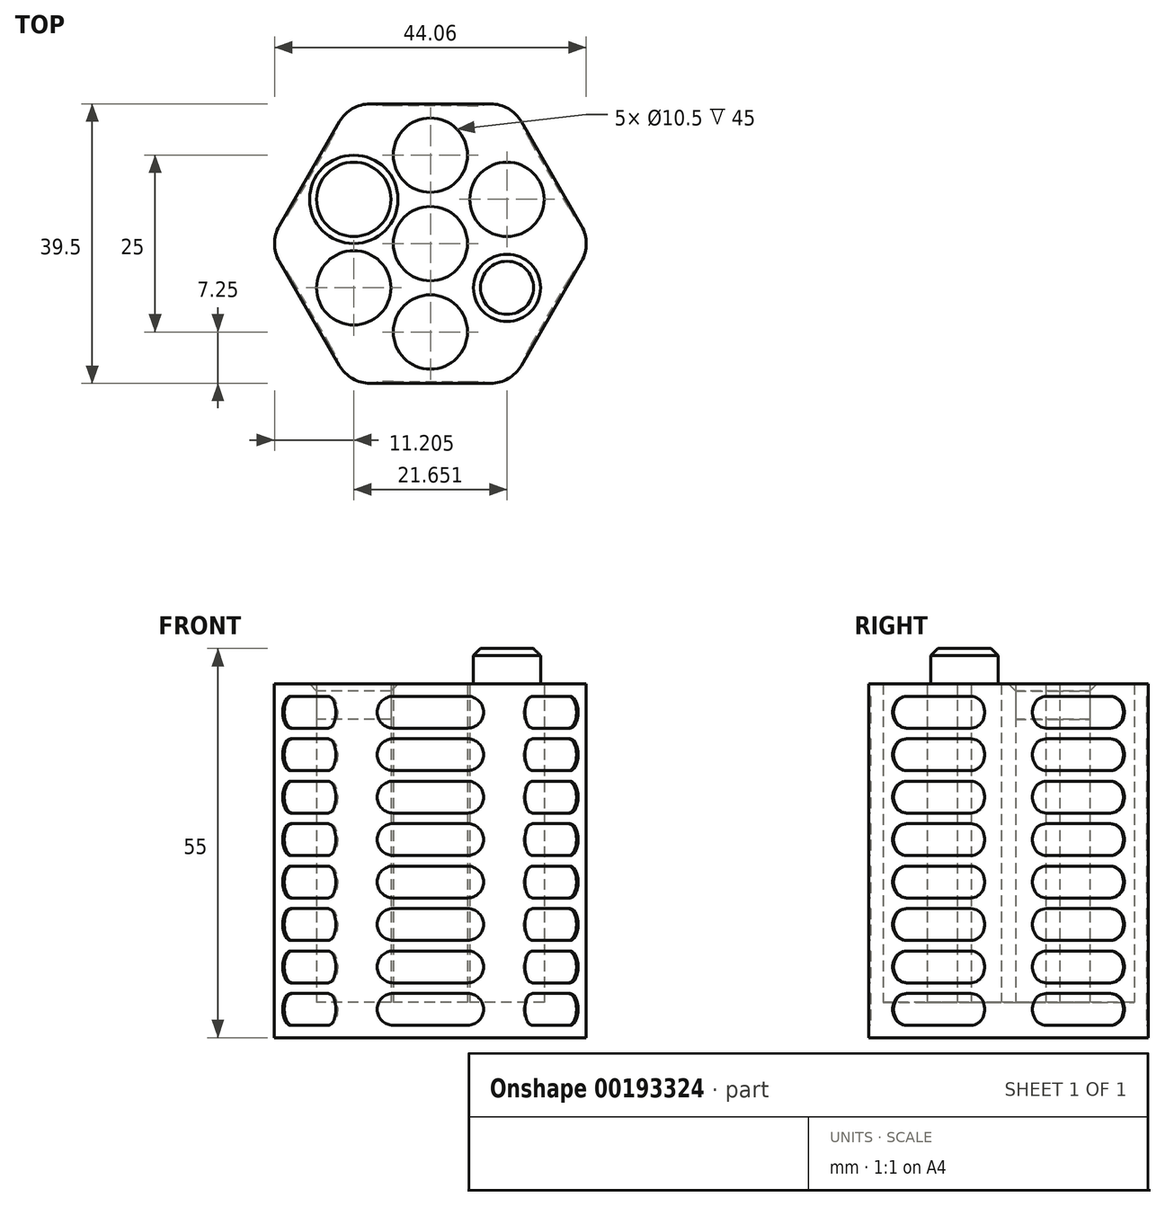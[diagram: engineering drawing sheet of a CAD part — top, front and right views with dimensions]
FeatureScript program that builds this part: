
annotation { "Feature Type Name" : "Feature", "Feature Type Description" : "" }
export const myFeature = defineFeature(function(context is Context, id is Id, definition is map)
    precondition{}
    {
        {
            var Q0;
            Q0=qCreatedBy(makeId("Top.planeOp"),FACE);
            var sketch = newSketch(context, id + "F0", { "sketchPlane" : qUnion([Q0])});
            skPoint(sketch, "E0.0.midPoint", {"position": v(0, 19.75) * mm});
            skCircle(sketch, "E1", {"center": v(0, 12.5) * mm, "radius": 5.25 * mm});
            skPoint(sketch, "E2.center", {"position": v(0, -4.69) * mm});
            skCircle(sketch, "E3.1.0", {"center": v(-10.83, 6.25) * mm, "radius": 5.25 * mm});
            skCircle(sketch, "E3.2.0", {"center": v(-10.83, -6.25) * mm, "radius": 5.25 * mm});
            skCircle(sketch, "E3.3.0", {"center": v(0, -12.5) * mm, "radius": 5.25 * mm});
            skCircle(sketch, "E3.4.0", {"center": v(10.83, -6.25) * mm, "radius": 4.75 * mm});
            skCircle(sketch, "E3.5.0", {"center": v(10.83, 6.25) * mm, "radius": 5.25 * mm});
            skPoint(sketch, "E3.center", {"position": v(0, 0) * mm});
            skCircle(sketch, "E4", {"center": v(0, 0) * mm, "radius": 5.25 * mm});
            skCircle(sketch, "E5.cCircle", {"center": v(0, 0) * mm, "radius": 19.75 * mm, "construction": true});
            skLineSegment(sketch, "E5.0", {"start": v(-11.4, 19.75) * mm, "end": v(11.4, 19.75) * mm});
            skLineSegment(sketch, "E5.1", {"start": v(11.4, 19.75) * mm, "end": v(22.8, 0) * mm});
            skLineSegment(sketch, "E5.2", {"start": v(22.8, 0) * mm, "end": v(11.4, -19.75) * mm});
            skLineSegment(sketch, "E5.3", {"start": v(11.4, -19.75) * mm, "end": v(-11.4, -19.75) * mm});
            skLineSegment(sketch, "E5.4", {"start": v(-11.4, -19.75) * mm, "end": v(-22.8, 0) * mm});
            skLineSegment(sketch, "E5.5", {"start": v(-22.8, 0) * mm, "end": v(-11.4, 19.75) * mm});
            skSolve(sketch);
        }
        {
            var Q0;
            Q0=makeQuery(id+"F0.imprint","IMPRINT",FACE,{"disambiguationData":[TD([[makeQuery(id+"F0.imprint","IMPRINT",EDGE,{"derivedFrom":sQuery(id+"F0.wireOp",EDGE,"E1")}),-1.0]])]});
            extrude(context, id + "F1", {"entities" : qUnion([Q0]), "depth" : 50 * mm});
        }
        {
            var Q0;
            Q0=makeQuery(id+"F0.imprint","IMPRINT",FACE,{"disambiguationData":[TD([[makeQuery(id+"F0.imprint","IMPRINT",EDGE,{"derivedFrom":sQuery(id+"F0.wireOp",EDGE,"E4")}),1.0]])]});
            var Q1;
            Q1=makeQuery(id+"F0.imprint","IMPRINT",FACE,{"disambiguationData":[TD([[makeQuery(id+"F0.imprint","IMPRINT",EDGE,{"derivedFrom":sQuery(id+"F0.wireOp",EDGE,"E1")}),1.0]])]});
            var Q2;
            Q2=makeQuery(id+"F0.imprint","IMPRINT",FACE,{"disambiguationData":[TD([[makeQuery(id+"F0.imprint","IMPRINT",EDGE,{"derivedFrom":sQuery(id+"F0.wireOp",EDGE,"E3.2.0")}),1.0]])]});
            var Q3;
            Q3=makeQuery(id+"F0.imprint","IMPRINT",FACE,{"disambiguationData":[TD([[makeQuery(id+"F0.imprint","IMPRINT",EDGE,{"derivedFrom":sQuery(id+"F0.wireOp",EDGE,"E3.3.0")}),1.0]])]});
            var Q4;
            Q4=makeQuery(id+"F0.imprint","IMPRINT",FACE,{"disambiguationData":[TD([[makeQuery(id+"F0.imprint","IMPRINT",EDGE,{"derivedFrom":sQuery(id+"F0.wireOp",EDGE,"E3.5.0")}),1.0]])]});
            extrude(context, id + "F2", {"entities" : qUnion([Q0, Q1, Q2, Q3, Q4]), "operationType" : NewBodyOperationType.ADD, "depth" : 5 * mm});
        }
        {
            var Q0;
            Q0=makeQuery(id+"F0.imprint","IMPRINT",FACE,{"disambiguationData":[TD([[makeQuery(id+"F0.imprint","IMPRINT",EDGE,{"derivedFrom":sQuery(id+"F0.wireOp",EDGE,"E3.4.0")}),1.0]])]});
            extrude(context, id + "F3", {"entities" : qUnion([Q0]), "operationType" : NewBodyOperationType.ADD, "depth" : 55 * mm});
        }
        {
            var Q0;
            Q0=makeQuery(id+"F0.imprint","IMPRINT",FACE,{"disambiguationData":[TD([[makeQuery(id+"F0.imprint","IMPRINT",EDGE,{"derivedFrom":sQuery(id+"F0.wireOp",EDGE,"E3.1.0")}),1.0]])]});
            extrude(context, id + "F4", {"entities" : qUnion([Q0]), "operationType" : NewBodyOperationType.ADD, "depth" : 45 * mm});
        }
        {
            var Q0;
            Q0=makeQuery(id+"F3.opExtrude","CAP_EDGE",EDGE,{"disambiguationData":[OSD([sQuery(id+"F0.wireOp",EDGE,"E3.4.0")])],"isStart":false});
            var Q1;
            Q1=makeQuery(id+"F1.opExtrude","CAP_EDGE",EDGE,{"disambiguationData":[OSD([sQuery(id+"F0.wireOp",EDGE,"E3.1.0")])],"isStart":false});
            var Q2;
            Q2=makeQuery(id+"F1.opExtrude","CAP_EDGE",EDGE,{"disambiguationData":[OSD([sQuery(id+"F0.wireOp",EDGE,"E3.4.0")])],"isStart":false});
            chamfer(context, id + "F5", {"entities" : qUnion([Q0, Q1, Q2]), "width" : 1 * mm, "tangentPropagation" : true});
        }
        {
            var Q0;
            {var subQ0=sQuery(id+"F0.wireOp",EDGE,"E5.5");var subQ1=sQuery(id+"F0.wireOp",EDGE,"E5.0");Q0=makeQuery(id+"FrbD3DidOZEMZMG_1.boolean.opBoolean","MERGE",EDGE,{"derivedFrom":[makeQuery(id+"F1.opExtrude","SWEPT_EDGE",EDGE,{"disambiguationData":[OSD([subQ1,subQ0])]}),makeQuery(id+"FrbD3DidOZEMZMG_1.opExtrude","SWEPT_EDGE",EDGE,{"disambiguationData":[OSD([subQ1,subQ0])]})]});}
            var Q1;
            {var subQ0=sQuery(id+"F0.wireOp",EDGE,"E5.1");var subQ1=sQuery(id+"F0.wireOp",EDGE,"E5.0");Q1=makeQuery(id+"FrbD3DidOZEMZMG_1.boolean.opBoolean","MERGE",EDGE,{"derivedFrom":[makeQuery(id+"F1.opExtrude","SWEPT_EDGE",EDGE,{"disambiguationData":[OSD([subQ1,subQ0])]}),makeQuery(id+"FrbD3DidOZEMZMG_1.opExtrude","SWEPT_EDGE",EDGE,{"disambiguationData":[OSD([subQ1,subQ0])]})]});}
            var Q2;
            {var subQ0=sQuery(id+"F0.wireOp",EDGE,"E5.2");var subQ1=sQuery(id+"F0.wireOp",EDGE,"E5.1");Q2=makeQuery(id+"FrbD3DidOZEMZMG_1.boolean.opBoolean","MERGE",EDGE,{"derivedFrom":[makeQuery(id+"F1.opExtrude","SWEPT_EDGE",EDGE,{"disambiguationData":[OSD([subQ1,subQ0])]}),makeQuery(id+"FrbD3DidOZEMZMG_1.opExtrude","SWEPT_EDGE",EDGE,{"disambiguationData":[OSD([subQ1,subQ0])]})]});}
            var Q3;
            {var subQ0=sQuery(id+"F0.wireOp",EDGE,"E5.5");var subQ1=sQuery(id+"F0.wireOp",EDGE,"E5.4");Q3=makeQuery(id+"FrbD3DidOZEMZMG_1.boolean.opBoolean","MERGE",EDGE,{"derivedFrom":[makeQuery(id+"F1.opExtrude","SWEPT_EDGE",EDGE,{"disambiguationData":[OSD([subQ1,subQ0])]}),makeQuery(id+"FrbD3DidOZEMZMG_1.opExtrude","SWEPT_EDGE",EDGE,{"disambiguationData":[OSD([subQ1,subQ0])]})]});}
            var Q4;
            {var subQ0=sQuery(id+"F0.wireOp",EDGE,"E5.4");var subQ1=sQuery(id+"F0.wireOp",EDGE,"E5.3");Q4=makeQuery(id+"FrbD3DidOZEMZMG_1.boolean.opBoolean","MERGE",EDGE,{"derivedFrom":[makeQuery(id+"F1.opExtrude","SWEPT_EDGE",EDGE,{"disambiguationData":[OSD([subQ1,subQ0])]}),makeQuery(id+"FrbD3DidOZEMZMG_1.opExtrude","SWEPT_EDGE",EDGE,{"disambiguationData":[OSD([subQ1,subQ0])]})]});}
            var Q5;
            {var subQ0=sQuery(id+"F0.wireOp",EDGE,"E5.3");var subQ1=sQuery(id+"F0.wireOp",EDGE,"E5.2");Q5=makeQuery(id+"FrbD3DidOZEMZMG_1.boolean.opBoolean","MERGE",EDGE,{"derivedFrom":[makeQuery(id+"F1.opExtrude","SWEPT_EDGE",EDGE,{"disambiguationData":[OSD([subQ1,subQ0])]}),makeQuery(id+"FrbD3DidOZEMZMG_1.opExtrude","SWEPT_EDGE",EDGE,{"disambiguationData":[OSD([subQ1,subQ0])]})]});}
            fillet(context, id + "F6", {"entities" : qUnion([Q0, Q1, Q2, Q3, Q4, Q5]), "radius" : 5 * mm, "tangentPropagation" : true, "allowEdgeOverflow" : false});
        }
        {
            var Q0;
            {var subQ0=sQuery(id+"F0.wireOp",EDGE,"E5.3");Q0=makeQuery(id+"FrbD3DidOZEMZMG_1.boolean.opBoolean","MERGE",FACE,{"derivedFrom":[makeQuery(id+"F1.opExtrude","SWEPT_FACE",FACE,{"disambiguationData":[OSD([subQ0])]}),makeQuery(id+"FrbD3DidOZEMZMG_1.opExtrude","SWEPT_FACE",FACE,{"disambiguationData":[OSD([subQ0])]})]});}
            var sketch = newSketch(context, id + "F7", { "sketchPlane" : qUnion([Q0])});
            skLineSegment(sketch, "E6", {"start": v(-5.27, 48.25) * mm, "end": v(5.27, 48.25) * mm});
            skArc(sketch, "E7", {"start": v(5.27, 43.75) * mm, "mid": v(7.52, 46) * mm, "end": v(5.27, 48.25) * mm});
            skLineSegment(sketch, "E8", {"start": v(5.27, 43.75) * mm, "end": v(-5.27, 43.75) * mm});
            skArc(sketch, "E9", {"start": v(-5.27, 48.25) * mm, "mid": v(-7.52, 46) * mm, "end": v(-5.27, 43.75) * mm});
            skArc(sketch, "E10.0.1.0", {"start": v(-5.27, 42.25) * mm, "mid": v(-7.52, 40) * mm, "end": v(-5.27, 37.75) * mm});
            skLineSegment(sketch, "E10.0.1.1", {"start": v(-5.27, 42.25) * mm, "end": v(5.27, 42.25) * mm});
            skArc(sketch, "E10.0.1.2", {"start": v(5.27, 37.75) * mm, "mid": v(7.52, 40) * mm, "end": v(5.27, 42.25) * mm});
            skLineSegment(sketch, "E10.0.1.3", {"start": v(5.27, 37.75) * mm, "end": v(-5.27, 37.75) * mm});
            skArc(sketch, "E10.0.2.0", {"start": v(-5.27, 36.25) * mm, "mid": v(-7.52, 34) * mm, "end": v(-5.27, 31.75) * mm});
            skLineSegment(sketch, "E10.0.2.1", {"start": v(-5.27, 36.25) * mm, "end": v(5.27, 36.25) * mm});
            skArc(sketch, "E10.0.2.2", {"start": v(5.27, 31.75) * mm, "mid": v(7.52, 34) * mm, "end": v(5.27, 36.25) * mm});
            skLineSegment(sketch, "E10.0.2.3", {"start": v(5.27, 31.75) * mm, "end": v(-5.27, 31.75) * mm});
            skArc(sketch, "E10.0.3.0", {"start": v(-5.27, 30.25) * mm, "mid": v(-7.52, 28) * mm, "end": v(-5.27, 25.75) * mm});
            skLineSegment(sketch, "E10.0.3.1", {"start": v(-5.27, 30.25) * mm, "end": v(5.27, 30.25) * mm});
            skArc(sketch, "E10.0.3.2", {"start": v(5.27, 25.75) * mm, "mid": v(7.52, 28) * mm, "end": v(5.27, 30.25) * mm});
            skLineSegment(sketch, "E10.0.3.3", {"start": v(5.27, 25.75) * mm, "end": v(-5.27, 25.75) * mm});
            skArc(sketch, "E10.0.4.0", {"start": v(-5.27, 24.25) * mm, "mid": v(-7.52, 22) * mm, "end": v(-5.27, 19.75) * mm});
            skLineSegment(sketch, "E10.0.4.1", {"start": v(-5.27, 24.25) * mm, "end": v(5.27, 24.25) * mm});
            skArc(sketch, "E10.0.4.2", {"start": v(5.27, 19.75) * mm, "mid": v(7.52, 22) * mm, "end": v(5.27, 24.25) * mm});
            skLineSegment(sketch, "E10.0.4.3", {"start": v(5.27, 19.75) * mm, "end": v(-5.27, 19.75) * mm});
            skArc(sketch, "E10.0.5.0", {"start": v(-5.27, 18.25) * mm, "mid": v(-7.52, 16) * mm, "end": v(-5.27, 13.75) * mm});
            skLineSegment(sketch, "E10.0.5.1", {"start": v(-5.27, 18.25) * mm, "end": v(5.27, 18.25) * mm});
            skArc(sketch, "E10.0.5.2", {"start": v(5.27, 13.75) * mm, "mid": v(7.52, 16) * mm, "end": v(5.27, 18.25) * mm});
            skLineSegment(sketch, "E10.0.5.3", {"start": v(5.27, 13.75) * mm, "end": v(-5.27, 13.75) * mm});
            skArc(sketch, "E10.0.6.0", {"start": v(-5.27, 12.25) * mm, "mid": v(-7.52, 10) * mm, "end": v(-5.27, 7.75) * mm});
            skLineSegment(sketch, "E10.0.6.1", {"start": v(-5.27, 12.25) * mm, "end": v(5.27, 12.25) * mm});
            skArc(sketch, "E10.0.6.2", {"start": v(5.27, 7.75) * mm, "mid": v(7.52, 10) * mm, "end": v(5.27, 12.25) * mm});
            skLineSegment(sketch, "E10.0.6.3", {"start": v(5.27, 7.75) * mm, "end": v(-5.27, 7.75) * mm});
            skArc(sketch, "E10.0.7.0", {"start": v(-5.27, 6.25) * mm, "mid": v(-7.52, 4) * mm, "end": v(-5.27, 1.75) * mm});
            skLineSegment(sketch, "E10.0.7.1", {"start": v(-5.27, 6.25) * mm, "end": v(5.27, 6.25) * mm});
            skArc(sketch, "E10.0.7.2", {"start": v(5.27, 1.75) * mm, "mid": v(7.52, 4) * mm, "end": v(5.27, 6.25) * mm});
            skLineSegment(sketch, "E10.0.7.3", {"start": v(5.27, 1.75) * mm, "end": v(-5.27, 1.75) * mm});
            skLineSegment(sketch, "E10.direction1", {"start": v(-5.27, 43.75) * mm, "end": v(19.73, 43.75) * mm, "construction": true});
            skLineSegment(sketch, "E10.direction2", {"start": v(-5.27, 43.75) * mm, "end": v(-5.27, 37.75) * mm, "construction": true});
            skSolve(sketch);
        }
        {
            var Q0;
            Q0=makeQuery(id+"F7.imprint","IMPRINT",FACE,{"disambiguationData":[TD([[makeQuery(id+"F7.imprint","IMPRINT",EDGE,{"derivedFrom":sQuery(id+"F7.wireOp",EDGE,"E6")}),-1.0]])]});
            var Q1;
            Q1=makeQuery(id+"F7.imprint","IMPRINT",FACE,{"disambiguationData":[TD([[makeQuery(id+"F7.imprint","IMPRINT",EDGE,{"derivedFrom":sQuery(id+"F7.wireOp",EDGE,"E10.0.1.0")}),1.0]])]});
            var Q2;
            Q2=makeQuery(id+"F7.imprint","IMPRINT",FACE,{"disambiguationData":[TD([[makeQuery(id+"F7.imprint","IMPRINT",EDGE,{"derivedFrom":sQuery(id+"F7.wireOp",EDGE,"E10.0.2.0")}),1.0]])]});
            var Q3;
            Q3=makeQuery(id+"F7.imprint","IMPRINT",FACE,{"disambiguationData":[TD([[makeQuery(id+"F7.imprint","IMPRINT",EDGE,{"derivedFrom":sQuery(id+"F7.wireOp",EDGE,"E10.0.3.0")}),1.0]])]});
            var Q4;
            Q4=makeQuery(id+"F7.imprint","IMPRINT",FACE,{"disambiguationData":[TD([[makeQuery(id+"F7.imprint","IMPRINT",EDGE,{"derivedFrom":sQuery(id+"F7.wireOp",EDGE,"E10.0.4.0")}),1.0]])]});
            var Q5;
            Q5=makeQuery(id+"F7.imprint","IMPRINT",FACE,{"disambiguationData":[TD([[makeQuery(id+"F7.imprint","IMPRINT",EDGE,{"derivedFrom":sQuery(id+"F7.wireOp",EDGE,"E10.0.5.0")}),1.0]])]});
            var Q6;
            Q6=makeQuery(id+"F7.imprint","IMPRINT",FACE,{"disambiguationData":[TD([[makeQuery(id+"F7.imprint","IMPRINT",EDGE,{"derivedFrom":sQuery(id+"F7.wireOp",EDGE,"E10.0.6.0")}),1.0]])]});
            var Q7;
            Q7=makeQuery(id+"F7.imprint","IMPRINT",FACE,{"disambiguationData":[TD([[makeQuery(id+"F7.imprint","IMPRINT",EDGE,{"derivedFrom":sQuery(id+"F7.wireOp",EDGE,"E10.0.7.0")}),1.0]])]});
            extrude(context, id + "F8", {"entities" : qUnion([Q0, Q1, Q2, Q3, Q4, Q5, Q6, Q7]), "operationType" : NewBodyOperationType.REMOVE, "oppositeDirection" : true, "depth" : .25 * mm});
        }
        {
            var Q0;
            {var subQ0=sQuery(id+"F0.wireOp",EDGE,"E5.2");Q0=makeQuery(id+"FrbD3DidOZEMZMG_1.boolean.opBoolean","MERGE",FACE,{"derivedFrom":[makeQuery(id+"F1.opExtrude","SWEPT_FACE",FACE,{"disambiguationData":[OSD([subQ0])]}),makeQuery(id+"FrbD3DidOZEMZMG_1.opExtrude","SWEPT_FACE",FACE,{"disambiguationData":[OSD([subQ0])]})]});}
            var sketch = newSketch(context, id + "F9", { "sketchPlane" : qUnion([Q0])});
            skLineSegment(sketch, "E11", {"start": v(-5.27, 48.25) * mm, "end": v(5.27, 48.25) * mm});
            skArc(sketch, "E12", {"start": v(5.27, 43.75) * mm, "mid": v(7.52, 46) * mm, "end": v(5.27, 48.25) * mm});
            skLineSegment(sketch, "E13", {"start": v(5.27, 43.75) * mm, "end": v(-5.27, 43.75) * mm});
            skArc(sketch, "E14", {"start": v(-5.27, 48.25) * mm, "mid": v(-7.52, 46) * mm, "end": v(-5.27, 43.75) * mm});
            skArc(sketch, "E15.0.1.0", {"start": v(-5.27, 42.25) * mm, "mid": v(-7.52, 40) * mm, "end": v(-5.27, 37.75) * mm});
            skLineSegment(sketch, "E15.0.1.1", {"start": v(-5.27, 42.25) * mm, "end": v(5.27, 42.25) * mm});
            skArc(sketch, "E15.0.1.2", {"start": v(5.27, 37.75) * mm, "mid": v(7.52, 40) * mm, "end": v(5.27, 42.25) * mm});
            skLineSegment(sketch, "E15.0.1.3", {"start": v(5.27, 37.75) * mm, "end": v(-5.27, 37.75) * mm});
            skArc(sketch, "E15.0.2.0", {"start": v(-5.27, 36.25) * mm, "mid": v(-7.52, 34) * mm, "end": v(-5.27, 31.75) * mm});
            skLineSegment(sketch, "E15.0.2.1", {"start": v(-5.27, 36.25) * mm, "end": v(5.27, 36.25) * mm});
            skArc(sketch, "E15.0.2.2", {"start": v(5.27, 31.75) * mm, "mid": v(7.52, 34) * mm, "end": v(5.27, 36.25) * mm});
            skLineSegment(sketch, "E15.0.2.3", {"start": v(5.27, 31.75) * mm, "end": v(-5.27, 31.75) * mm});
            skArc(sketch, "E15.0.3.0", {"start": v(-5.27, 30.25) * mm, "mid": v(-7.52, 28) * mm, "end": v(-5.27, 25.75) * mm});
            skLineSegment(sketch, "E15.0.3.1", {"start": v(-5.27, 30.25) * mm, "end": v(5.27, 30.25) * mm});
            skArc(sketch, "E15.0.3.2", {"start": v(5.27, 25.75) * mm, "mid": v(7.52, 28) * mm, "end": v(5.27, 30.25) * mm});
            skLineSegment(sketch, "E15.0.3.3", {"start": v(5.27, 25.75) * mm, "end": v(-5.27, 25.75) * mm});
            skArc(sketch, "E15.0.4.0", {"start": v(-5.27, 24.25) * mm, "mid": v(-7.52, 22) * mm, "end": v(-5.27, 19.75) * mm});
            skLineSegment(sketch, "E15.0.4.1", {"start": v(-5.27, 24.25) * mm, "end": v(5.27, 24.25) * mm});
            skArc(sketch, "E15.0.4.2", {"start": v(5.27, 19.75) * mm, "mid": v(7.52, 22) * mm, "end": v(5.27, 24.25) * mm});
            skLineSegment(sketch, "E15.0.4.3", {"start": v(5.27, 19.75) * mm, "end": v(-5.27, 19.75) * mm});
            skArc(sketch, "E15.0.5.0", {"start": v(-5.27, 18.25) * mm, "mid": v(-7.52, 16) * mm, "end": v(-5.27, 13.75) * mm});
            skLineSegment(sketch, "E15.0.5.1", {"start": v(-5.27, 18.25) * mm, "end": v(5.27, 18.25) * mm});
            skArc(sketch, "E15.0.5.2", {"start": v(5.27, 13.75) * mm, "mid": v(7.52, 16) * mm, "end": v(5.27, 18.25) * mm});
            skLineSegment(sketch, "E15.0.5.3", {"start": v(5.27, 13.75) * mm, "end": v(-5.27, 13.75) * mm});
            skArc(sketch, "E15.0.6.0", {"start": v(-5.27, 12.25) * mm, "mid": v(-7.52, 10) * mm, "end": v(-5.27, 7.75) * mm});
            skLineSegment(sketch, "E15.0.6.1", {"start": v(-5.27, 12.25) * mm, "end": v(5.27, 12.25) * mm});
            skArc(sketch, "E15.0.6.2", {"start": v(5.27, 7.75) * mm, "mid": v(7.52, 10) * mm, "end": v(5.27, 12.25) * mm});
            skLineSegment(sketch, "E15.0.6.3", {"start": v(5.27, 7.75) * mm, "end": v(-5.27, 7.75) * mm});
            skArc(sketch, "E15.0.7.0", {"start": v(-5.27, 6.25) * mm, "mid": v(-7.52, 4) * mm, "end": v(-5.27, 1.75) * mm});
            skLineSegment(sketch, "E15.0.7.1", {"start": v(-5.27, 6.25) * mm, "end": v(5.27, 6.25) * mm});
            skArc(sketch, "E15.0.7.2", {"start": v(5.27, 1.75) * mm, "mid": v(7.52, 4) * mm, "end": v(5.27, 6.25) * mm});
            skLineSegment(sketch, "E15.0.7.3", {"start": v(5.27, 1.75) * mm, "end": v(-5.27, 1.75) * mm});
            skLineSegment(sketch, "E15.direction1", {"start": v(-5.27, 43.75) * mm, "end": v(20.73, 43.75) * mm, "construction": true});
            skLineSegment(sketch, "E15.direction2", {"start": v(-5.27, 43.75) * mm, "end": v(-5.27, 37.75) * mm, "construction": true});
            skSolve(sketch);
        }
        {
            var Q0;
            Q0=makeQuery(id+"F9.imprint","IMPRINT",FACE,{"disambiguationData":[TD([[makeQuery(id+"F9.imprint","IMPRINT",EDGE,{"derivedFrom":sQuery(id+"F9.wireOp",EDGE,"E11")}),-1.0]])]});
            var Q1;
            Q1=makeQuery(id+"F9.imprint","IMPRINT",FACE,{"disambiguationData":[TD([[makeQuery(id+"F9.imprint","IMPRINT",EDGE,{"derivedFrom":sQuery(id+"F9.wireOp",EDGE,"E15.0.1.0")}),1.0]])]});
            var Q2;
            Q2=makeQuery(id+"F9.imprint","IMPRINT",FACE,{"disambiguationData":[TD([[makeQuery(id+"F9.imprint","IMPRINT",EDGE,{"derivedFrom":sQuery(id+"F9.wireOp",EDGE,"E15.0.2.0")}),1.0]])]});
            var Q3;
            Q3=makeQuery(id+"F9.imprint","IMPRINT",FACE,{"disambiguationData":[TD([[makeQuery(id+"F9.imprint","IMPRINT",EDGE,{"derivedFrom":sQuery(id+"F9.wireOp",EDGE,"E15.0.3.0")}),1.0]])]});
            var Q4;
            Q4=makeQuery(id+"F9.imprint","IMPRINT",FACE,{"disambiguationData":[TD([[makeQuery(id+"F9.imprint","IMPRINT",EDGE,{"derivedFrom":sQuery(id+"F9.wireOp",EDGE,"E15.0.4.0")}),1.0]])]});
            var Q5;
            Q5=makeQuery(id+"F9.imprint","IMPRINT",FACE,{"disambiguationData":[TD([[makeQuery(id+"F9.imprint","IMPRINT",EDGE,{"derivedFrom":sQuery(id+"F9.wireOp",EDGE,"E15.0.5.0")}),1.0]])]});
            var Q6;
            Q6=makeQuery(id+"F9.imprint","IMPRINT",FACE,{"disambiguationData":[TD([[makeQuery(id+"F9.imprint","IMPRINT",EDGE,{"derivedFrom":sQuery(id+"F9.wireOp",EDGE,"E15.0.6.0")}),1.0]])]});
            var Q7;
            Q7=makeQuery(id+"F9.imprint","IMPRINT",FACE,{"disambiguationData":[TD([[makeQuery(id+"F9.imprint","IMPRINT",EDGE,{"derivedFrom":sQuery(id+"F9.wireOp",EDGE,"E15.0.7.0")}),1.0]])]});
            extrude(context, id + "F10", {"entities" : qUnion([Q0, Q1, Q2, Q3, Q4, Q5, Q6, Q7]), "operationType" : NewBodyOperationType.REMOVE, "oppositeDirection" : true, "depth" : .25 * mm});
        }
        {
            var Q0;
            {var subQ0=sQuery(id+"F0.wireOp",EDGE,"E5.1");Q0=makeQuery(id+"FrbD3DidOZEMZMG_1.boolean.opBoolean","MERGE",FACE,{"derivedFrom":[makeQuery(id+"F1.opExtrude","SWEPT_FACE",FACE,{"disambiguationData":[OSD([subQ0])]}),makeQuery(id+"FrbD3DidOZEMZMG_1.opExtrude","SWEPT_FACE",FACE,{"disambiguationData":[OSD([subQ0])]})]});}
            var sketch = newSketch(context, id + "F11", { "sketchPlane" : qUnion([Q0])});
            skLineSegment(sketch, "E16", {"start": v(-5.27, 48.25) * mm, "end": v(5.27, 48.25) * mm});
            skArc(sketch, "E17", {"start": v(5.27, 43.75) * mm, "mid": v(7.52, 46) * mm, "end": v(5.27, 48.25) * mm});
            skLineSegment(sketch, "E18", {"start": v(5.27, 43.75) * mm, "end": v(-5.27, 43.75) * mm});
            skArc(sketch, "E19", {"start": v(-5.27, 48.25) * mm, "mid": v(-7.52, 46) * mm, "end": v(-5.27, 43.75) * mm});
            skArc(sketch, "E20.0.1.0", {"start": v(-5.27, 42.25) * mm, "mid": v(-7.52, 40) * mm, "end": v(-5.27, 37.75) * mm});
            skLineSegment(sketch, "E20.0.1.1", {"start": v(-5.27, 42.25) * mm, "end": v(5.27, 42.25) * mm});
            skArc(sketch, "E20.0.1.2", {"start": v(5.27, 37.75) * mm, "mid": v(7.52, 40) * mm, "end": v(5.27, 42.25) * mm});
            skLineSegment(sketch, "E20.0.1.3", {"start": v(5.27, 37.75) * mm, "end": v(-5.27, 37.75) * mm});
            skArc(sketch, "E20.0.2.0", {"start": v(-5.27, 36.25) * mm, "mid": v(-7.52, 34) * mm, "end": v(-5.27, 31.75) * mm});
            skLineSegment(sketch, "E20.0.2.1", {"start": v(-5.27, 36.25) * mm, "end": v(5.27, 36.25) * mm});
            skArc(sketch, "E20.0.2.2", {"start": v(5.27, 31.75) * mm, "mid": v(7.52, 34) * mm, "end": v(5.27, 36.25) * mm});
            skLineSegment(sketch, "E20.0.2.3", {"start": v(5.27, 31.75) * mm, "end": v(-5.27, 31.75) * mm});
            skArc(sketch, "E20.0.3.0", {"start": v(-5.27, 30.25) * mm, "mid": v(-7.52, 28) * mm, "end": v(-5.27, 25.75) * mm});
            skLineSegment(sketch, "E20.0.3.1", {"start": v(-5.27, 30.25) * mm, "end": v(5.27, 30.25) * mm});
            skArc(sketch, "E20.0.3.2", {"start": v(5.27, 25.75) * mm, "mid": v(7.52, 28) * mm, "end": v(5.27, 30.25) * mm});
            skLineSegment(sketch, "E20.0.3.3", {"start": v(5.27, 25.75) * mm, "end": v(-5.27, 25.75) * mm});
            skArc(sketch, "E20.0.4.0", {"start": v(-5.27, 24.25) * mm, "mid": v(-7.52, 22) * mm, "end": v(-5.27, 19.75) * mm});
            skLineSegment(sketch, "E20.0.4.1", {"start": v(-5.27, 24.25) * mm, "end": v(5.27, 24.25) * mm});
            skArc(sketch, "E20.0.4.2", {"start": v(5.27, 19.75) * mm, "mid": v(7.52, 22) * mm, "end": v(5.27, 24.25) * mm});
            skLineSegment(sketch, "E20.0.4.3", {"start": v(5.27, 19.75) * mm, "end": v(-5.27, 19.75) * mm});
            skArc(sketch, "E20.0.5.0", {"start": v(-5.27, 18.25) * mm, "mid": v(-7.52, 16) * mm, "end": v(-5.27, 13.75) * mm});
            skLineSegment(sketch, "E20.0.5.1", {"start": v(-5.27, 18.25) * mm, "end": v(5.27, 18.25) * mm});
            skArc(sketch, "E20.0.5.2", {"start": v(5.27, 13.75) * mm, "mid": v(7.52, 16) * mm, "end": v(5.27, 18.25) * mm});
            skLineSegment(sketch, "E20.0.5.3", {"start": v(5.27, 13.75) * mm, "end": v(-5.27, 13.75) * mm});
            skArc(sketch, "E20.0.6.0", {"start": v(-5.27, 12.25) * mm, "mid": v(-7.52, 10) * mm, "end": v(-5.27, 7.75) * mm});
            skLineSegment(sketch, "E20.0.6.1", {"start": v(-5.27, 12.25) * mm, "end": v(5.27, 12.25) * mm});
            skArc(sketch, "E20.0.6.2", {"start": v(5.27, 7.75) * mm, "mid": v(7.52, 10) * mm, "end": v(5.27, 12.25) * mm});
            skLineSegment(sketch, "E20.0.6.3", {"start": v(5.27, 7.75) * mm, "end": v(-5.27, 7.75) * mm});
            skArc(sketch, "E20.0.7.0", {"start": v(-5.27, 6.25) * mm, "mid": v(-7.52, 4) * mm, "end": v(-5.27, 1.75) * mm});
            skLineSegment(sketch, "E20.0.7.1", {"start": v(-5.27, 6.25) * mm, "end": v(5.27, 6.25) * mm});
            skArc(sketch, "E20.0.7.2", {"start": v(5.27, 1.75) * mm, "mid": v(7.52, 4) * mm, "end": v(5.27, 6.25) * mm});
            skLineSegment(sketch, "E20.0.7.3", {"start": v(5.27, 1.75) * mm, "end": v(-5.27, 1.75) * mm});
            skLineSegment(sketch, "E20.direction1", {"start": v(-5.27, 43.75) * mm, "end": v(16.53, 43.75) * mm, "construction": true});
            skLineSegment(sketch, "E20.direction2", {"start": v(-5.27, 43.75) * mm, "end": v(-5.27, 37.75) * mm, "construction": true});
            skSolve(sketch);
        }
        {
            var Q0;
            Q0=makeQuery(id+"F11.imprint","IMPRINT",FACE,{"disambiguationData":[TD([[makeQuery(id+"F11.imprint","IMPRINT",EDGE,{"derivedFrom":sQuery(id+"F11.wireOp",EDGE,"E16")}),-1.0]])]});
            var Q1;
            Q1=makeQuery(id+"F11.imprint","IMPRINT",FACE,{"disambiguationData":[TD([[makeQuery(id+"F11.imprint","IMPRINT",EDGE,{"derivedFrom":sQuery(id+"F11.wireOp",EDGE,"E20.0.1.0")}),1.0]])]});
            var Q2;
            Q2=makeQuery(id+"F11.imprint","IMPRINT",FACE,{"disambiguationData":[TD([[makeQuery(id+"F11.imprint","IMPRINT",EDGE,{"derivedFrom":sQuery(id+"F11.wireOp",EDGE,"E20.0.2.0")}),1.0]])]});
            var Q3;
            Q3=makeQuery(id+"F11.imprint","IMPRINT",FACE,{"disambiguationData":[TD([[makeQuery(id+"F11.imprint","IMPRINT",EDGE,{"derivedFrom":sQuery(id+"F11.wireOp",EDGE,"E20.0.3.0")}),1.0]])]});
            var Q4;
            Q4=makeQuery(id+"F11.imprint","IMPRINT",FACE,{"disambiguationData":[TD([[makeQuery(id+"F11.imprint","IMPRINT",EDGE,{"derivedFrom":sQuery(id+"F11.wireOp",EDGE,"E20.0.4.0")}),1.0]])]});
            var Q5;
            Q5=makeQuery(id+"F11.imprint","IMPRINT",FACE,{"disambiguationData":[TD([[makeQuery(id+"F11.imprint","IMPRINT",EDGE,{"derivedFrom":sQuery(id+"F11.wireOp",EDGE,"E20.0.5.0")}),1.0]])]});
            var Q6;
            Q6=makeQuery(id+"F11.imprint","IMPRINT",FACE,{"disambiguationData":[TD([[makeQuery(id+"F11.imprint","IMPRINT",EDGE,{"derivedFrom":sQuery(id+"F11.wireOp",EDGE,"E20.0.6.0")}),1.0]])]});
            var Q7;
            Q7=makeQuery(id+"F11.imprint","IMPRINT",FACE,{"disambiguationData":[TD([[makeQuery(id+"F11.imprint","IMPRINT",EDGE,{"derivedFrom":sQuery(id+"F11.wireOp",EDGE,"E20.0.7.0")}),1.0]])]});
            extrude(context, id + "F12", {"entities" : qUnion([Q0, Q1, Q2, Q3, Q4, Q5, Q6, Q7]), "operationType" : NewBodyOperationType.REMOVE, "oppositeDirection" : true, "depth" : .25 * mm});
        }
        {
            var Q0;
            {var subQ0=sQuery(id+"F0.wireOp",EDGE,"E5.0");Q0=makeQuery(id+"FrbD3DidOZEMZMG_1.boolean.opBoolean","MERGE",FACE,{"derivedFrom":[makeQuery(id+"F1.opExtrude","SWEPT_FACE",FACE,{"disambiguationData":[OSD([subQ0])]}),makeQuery(id+"FrbD3DidOZEMZMG_1.opExtrude","SWEPT_FACE",FACE,{"disambiguationData":[OSD([subQ0])]})]});}
            var sketch = newSketch(context, id + "F13", { "sketchPlane" : qUnion([Q0])});
            skLineSegment(sketch, "E21", {"start": v(-5.27, 48.25) * mm, "end": v(5.27, 48.25) * mm});
            skArc(sketch, "E22", {"start": v(5.27, 43.75) * mm, "mid": v(7.52, 46) * mm, "end": v(5.27, 48.25) * mm});
            skLineSegment(sketch, "E23", {"start": v(5.27, 43.75) * mm, "end": v(-5.27, 43.75) * mm});
            skArc(sketch, "E24", {"start": v(-5.27, 48.25) * mm, "mid": v(-7.52, 46) * mm, "end": v(-5.27, 43.75) * mm});
            skArc(sketch, "E25.0.1.0", {"start": v(-5.27, 42.25) * mm, "mid": v(-7.52, 40) * mm, "end": v(-5.27, 37.75) * mm});
            skLineSegment(sketch, "E25.0.1.1", {"start": v(-5.27, 42.25) * mm, "end": v(5.27, 42.25) * mm});
            skArc(sketch, "E25.0.1.2", {"start": v(5.27, 37.75) * mm, "mid": v(7.52, 40) * mm, "end": v(5.27, 42.25) * mm});
            skLineSegment(sketch, "E25.0.1.3", {"start": v(5.27, 37.75) * mm, "end": v(-5.27, 37.75) * mm});
            skArc(sketch, "E25.0.2.0", {"start": v(-5.27, 36.25) * mm, "mid": v(-7.52, 34) * mm, "end": v(-5.27, 31.75) * mm});
            skLineSegment(sketch, "E25.0.2.1", {"start": v(-5.27, 36.25) * mm, "end": v(5.27, 36.25) * mm});
            skArc(sketch, "E25.0.2.2", {"start": v(5.27, 31.75) * mm, "mid": v(7.52, 34) * mm, "end": v(5.27, 36.25) * mm});
            skLineSegment(sketch, "E25.0.2.3", {"start": v(5.27, 31.75) * mm, "end": v(-5.27, 31.75) * mm});
            skArc(sketch, "E25.0.3.0", {"start": v(-5.27, 30.25) * mm, "mid": v(-7.52, 28) * mm, "end": v(-5.27, 25.75) * mm});
            skLineSegment(sketch, "E25.0.3.1", {"start": v(-5.27, 30.25) * mm, "end": v(5.27, 30.25) * mm});
            skArc(sketch, "E25.0.3.2", {"start": v(5.27, 25.75) * mm, "mid": v(7.52, 28) * mm, "end": v(5.27, 30.25) * mm});
            skLineSegment(sketch, "E25.0.3.3", {"start": v(5.27, 25.75) * mm, "end": v(-5.27, 25.75) * mm});
            skArc(sketch, "E25.0.4.0", {"start": v(-5.27, 24.25) * mm, "mid": v(-7.52, 22) * mm, "end": v(-5.27, 19.75) * mm});
            skLineSegment(sketch, "E25.0.4.1", {"start": v(-5.27, 24.25) * mm, "end": v(5.27, 24.25) * mm});
            skArc(sketch, "E25.0.4.2", {"start": v(5.27, 19.75) * mm, "mid": v(7.52, 22) * mm, "end": v(5.27, 24.25) * mm});
            skLineSegment(sketch, "E25.0.4.3", {"start": v(5.27, 19.75) * mm, "end": v(-5.27, 19.75) * mm});
            skArc(sketch, "E25.0.5.0", {"start": v(-5.27, 18.25) * mm, "mid": v(-7.52, 16) * mm, "end": v(-5.27, 13.75) * mm});
            skLineSegment(sketch, "E25.0.5.1", {"start": v(-5.27, 18.25) * mm, "end": v(5.27, 18.25) * mm});
            skArc(sketch, "E25.0.5.2", {"start": v(5.27, 13.75) * mm, "mid": v(7.52, 16) * mm, "end": v(5.27, 18.25) * mm});
            skLineSegment(sketch, "E25.0.5.3", {"start": v(5.27, 13.75) * mm, "end": v(-5.27, 13.75) * mm});
            skArc(sketch, "E25.0.6.0", {"start": v(-5.27, 12.25) * mm, "mid": v(-7.52, 10) * mm, "end": v(-5.27, 7.75) * mm});
            skLineSegment(sketch, "E25.0.6.1", {"start": v(-5.27, 12.25) * mm, "end": v(5.27, 12.25) * mm});
            skArc(sketch, "E25.0.6.2", {"start": v(5.27, 7.75) * mm, "mid": v(7.52, 10) * mm, "end": v(5.27, 12.25) * mm});
            skLineSegment(sketch, "E25.0.6.3", {"start": v(5.27, 7.75) * mm, "end": v(-5.27, 7.75) * mm});
            skArc(sketch, "E25.0.7.0", {"start": v(-5.27, 6.25) * mm, "mid": v(-7.52, 4) * mm, "end": v(-5.27, 1.75) * mm});
            skLineSegment(sketch, "E25.0.7.1", {"start": v(-5.27, 6.25) * mm, "end": v(5.27, 6.25) * mm});
            skArc(sketch, "E25.0.7.2", {"start": v(5.27, 1.75) * mm, "mid": v(7.52, 4) * mm, "end": v(5.27, 6.25) * mm});
            skLineSegment(sketch, "E25.0.7.3", {"start": v(5.27, 1.75) * mm, "end": v(-5.27, 1.75) * mm});
            skLineSegment(sketch, "E25.direction1", {"start": v(-5.27, 43.75) * mm, "end": v(19.3, 43.75) * mm, "construction": true});
            skLineSegment(sketch, "E25.direction2", {"start": v(-5.27, 43.75) * mm, "end": v(-5.27, 37.75) * mm, "construction": true});
            skSolve(sketch);
        }
        {
            var Q0;
            Q0=makeQuery(id+"F13.imprint","IMPRINT",FACE,{"disambiguationData":[TD([[makeQuery(id+"F13.imprint","IMPRINT",EDGE,{"derivedFrom":sQuery(id+"F13.wireOp",EDGE,"E21")}),-1.0]])]});
            var Q1;
            Q1=makeQuery(id+"F13.imprint","IMPRINT",FACE,{"disambiguationData":[TD([[makeQuery(id+"F13.imprint","IMPRINT",EDGE,{"derivedFrom":sQuery(id+"F13.wireOp",EDGE,"E25.0.1.0")}),1.0]])]});
            var Q2;
            Q2=makeQuery(id+"F13.imprint","IMPRINT",FACE,{"disambiguationData":[TD([[makeQuery(id+"F13.imprint","IMPRINT",EDGE,{"derivedFrom":sQuery(id+"F13.wireOp",EDGE,"E25.0.2.0")}),1.0]])]});
            var Q3;
            Q3=makeQuery(id+"F13.imprint","IMPRINT",FACE,{"disambiguationData":[TD([[makeQuery(id+"F13.imprint","IMPRINT",EDGE,{"derivedFrom":sQuery(id+"F13.wireOp",EDGE,"E25.0.3.0")}),1.0]])]});
            var Q4;
            Q4=makeQuery(id+"F13.imprint","IMPRINT",FACE,{"disambiguationData":[TD([[makeQuery(id+"F13.imprint","IMPRINT",EDGE,{"derivedFrom":sQuery(id+"F13.wireOp",EDGE,"E25.0.4.0")}),1.0]])]});
            var Q5;
            Q5=makeQuery(id+"F13.imprint","IMPRINT",FACE,{"disambiguationData":[TD([[makeQuery(id+"F13.imprint","IMPRINT",EDGE,{"derivedFrom":sQuery(id+"F13.wireOp",EDGE,"E25.0.5.0")}),1.0]])]});
            var Q6;
            Q6=makeQuery(id+"F13.imprint","IMPRINT",FACE,{"disambiguationData":[TD([[makeQuery(id+"F13.imprint","IMPRINT",EDGE,{"derivedFrom":sQuery(id+"F13.wireOp",EDGE,"E25.0.6.0")}),1.0]])]});
            var Q7;
            Q7=makeQuery(id+"F13.imprint","IMPRINT",FACE,{"disambiguationData":[TD([[makeQuery(id+"F13.imprint","IMPRINT",EDGE,{"derivedFrom":sQuery(id+"F13.wireOp",EDGE,"E25.0.7.0")}),1.0]])]});
            extrude(context, id + "F14", {"entities" : qUnion([Q0, Q1, Q2, Q3, Q4, Q5, Q6, Q7]), "operationType" : NewBodyOperationType.REMOVE, "oppositeDirection" : true, "depth" : .25 * mm});
        }
        {
            var Q0;
            {var subQ0=sQuery(id+"F0.wireOp",EDGE,"E5.5");Q0=makeQuery(id+"FrbD3DidOZEMZMG_1.boolean.opBoolean","MERGE",FACE,{"derivedFrom":[makeQuery(id+"F1.opExtrude","SWEPT_FACE",FACE,{"disambiguationData":[OSD([subQ0])]}),makeQuery(id+"FrbD3DidOZEMZMG_1.opExtrude","SWEPT_FACE",FACE,{"disambiguationData":[OSD([subQ0])]})]});}
            var sketch = newSketch(context, id + "F15", { "sketchPlane" : qUnion([Q0])});
            skLineSegment(sketch, "E26", {"start": v(-5.27, 48.25) * mm, "end": v(5.27, 48.25) * mm});
            skArc(sketch, "E27", {"start": v(5.27, 43.75) * mm, "mid": v(7.52, 46) * mm, "end": v(5.27, 48.25) * mm});
            skLineSegment(sketch, "E28", {"start": v(5.27, 43.75) * mm, "end": v(-5.27, 43.75) * mm});
            skArc(sketch, "E29", {"start": v(-5.27, 48.25) * mm, "mid": v(-7.52, 46) * mm, "end": v(-5.27, 43.75) * mm});
            skArc(sketch, "E30.0.1.0", {"start": v(-5.27, 42.25) * mm, "mid": v(-7.52, 40) * mm, "end": v(-5.27, 37.75) * mm});
            skLineSegment(sketch, "E30.0.1.1", {"start": v(-5.27, 42.25) * mm, "end": v(5.27, 42.25) * mm});
            skArc(sketch, "E30.0.1.2", {"start": v(5.27, 37.75) * mm, "mid": v(7.52, 40) * mm, "end": v(5.27, 42.25) * mm});
            skLineSegment(sketch, "E30.0.1.3", {"start": v(5.27, 37.75) * mm, "end": v(-5.27, 37.75) * mm});
            skArc(sketch, "E30.0.2.0", {"start": v(-5.27, 36.25) * mm, "mid": v(-7.52, 34) * mm, "end": v(-5.27, 31.75) * mm});
            skLineSegment(sketch, "E30.0.2.1", {"start": v(-5.27, 36.25) * mm, "end": v(5.27, 36.25) * mm});
            skArc(sketch, "E30.0.2.2", {"start": v(5.27, 31.75) * mm, "mid": v(7.52, 34) * mm, "end": v(5.27, 36.25) * mm});
            skLineSegment(sketch, "E30.0.2.3", {"start": v(5.27, 31.75) * mm, "end": v(-5.27, 31.75) * mm});
            skArc(sketch, "E30.0.3.0", {"start": v(-5.27, 30.25) * mm, "mid": v(-7.52, 28) * mm, "end": v(-5.27, 25.75) * mm});
            skLineSegment(sketch, "E30.0.3.1", {"start": v(-5.27, 30.25) * mm, "end": v(5.27, 30.25) * mm});
            skArc(sketch, "E30.0.3.2", {"start": v(5.27, 25.75) * mm, "mid": v(7.52, 28) * mm, "end": v(5.27, 30.25) * mm});
            skLineSegment(sketch, "E30.0.3.3", {"start": v(5.27, 25.75) * mm, "end": v(-5.27, 25.75) * mm});
            skArc(sketch, "E30.0.4.0", {"start": v(-5.27, 24.25) * mm, "mid": v(-7.52, 22) * mm, "end": v(-5.27, 19.75) * mm});
            skLineSegment(sketch, "E30.0.4.1", {"start": v(-5.27, 24.25) * mm, "end": v(5.27, 24.25) * mm});
            skArc(sketch, "E30.0.4.2", {"start": v(5.27, 19.75) * mm, "mid": v(7.52, 22) * mm, "end": v(5.27, 24.25) * mm});
            skLineSegment(sketch, "E30.0.4.3", {"start": v(5.27, 19.75) * mm, "end": v(-5.27, 19.75) * mm});
            skArc(sketch, "E30.0.5.0", {"start": v(-5.27, 18.25) * mm, "mid": v(-7.52, 16) * mm, "end": v(-5.27, 13.75) * mm});
            skLineSegment(sketch, "E30.0.5.1", {"start": v(-5.27, 18.25) * mm, "end": v(5.27, 18.25) * mm});
            skArc(sketch, "E30.0.5.2", {"start": v(5.27, 13.75) * mm, "mid": v(7.52, 16) * mm, "end": v(5.27, 18.25) * mm});
            skLineSegment(sketch, "E30.0.5.3", {"start": v(5.27, 13.75) * mm, "end": v(-5.27, 13.75) * mm});
            skArc(sketch, "E30.0.6.0", {"start": v(-5.27, 12.25) * mm, "mid": v(-7.52, 10) * mm, "end": v(-5.27, 7.75) * mm});
            skLineSegment(sketch, "E30.0.6.1", {"start": v(-5.27, 12.25) * mm, "end": v(5.27, 12.25) * mm});
            skArc(sketch, "E30.0.6.2", {"start": v(5.27, 7.75) * mm, "mid": v(7.52, 10) * mm, "end": v(5.27, 12.25) * mm});
            skLineSegment(sketch, "E30.0.6.3", {"start": v(5.27, 7.75) * mm, "end": v(-5.27, 7.75) * mm});
            skArc(sketch, "E30.0.7.0", {"start": v(-5.27, 6.25) * mm, "mid": v(-7.52, 4) * mm, "end": v(-5.27, 1.75) * mm});
            skLineSegment(sketch, "E30.0.7.1", {"start": v(-5.27, 6.25) * mm, "end": v(5.27, 6.25) * mm});
            skArc(sketch, "E30.0.7.2", {"start": v(5.27, 1.75) * mm, "mid": v(7.52, 4) * mm, "end": v(5.27, 6.25) * mm});
            skLineSegment(sketch, "E30.0.7.3", {"start": v(5.27, 1.75) * mm, "end": v(-5.27, 1.75) * mm});
            skLineSegment(sketch, "E30.direction1", {"start": v(-5.27, 43.75) * mm, "end": v(16.64, 43.75) * mm, "construction": true});
            skLineSegment(sketch, "E30.direction2", {"start": v(-5.27, 43.75) * mm, "end": v(-5.27, 37.75) * mm, "construction": true});
            skSolve(sketch);
        }
        {
            var Q0;
            Q0=makeQuery(id+"F15.imprint","IMPRINT",FACE,{"disambiguationData":[TD([[makeQuery(id+"F15.imprint","IMPRINT",EDGE,{"derivedFrom":sQuery(id+"F15.wireOp",EDGE,"E26")}),-1.0]])]});
            var Q1;
            Q1=makeQuery(id+"F15.imprint","IMPRINT",FACE,{"disambiguationData":[TD([[makeQuery(id+"F15.imprint","IMPRINT",EDGE,{"derivedFrom":sQuery(id+"F15.wireOp",EDGE,"E30.0.1.0")}),1.0]])]});
            var Q2;
            Q2=makeQuery(id+"F15.imprint","IMPRINT",FACE,{"disambiguationData":[TD([[makeQuery(id+"F15.imprint","IMPRINT",EDGE,{"derivedFrom":sQuery(id+"F15.wireOp",EDGE,"E30.0.2.0")}),1.0]])]});
            var Q3;
            Q3=makeQuery(id+"F15.imprint","IMPRINT",FACE,{"disambiguationData":[TD([[makeQuery(id+"F15.imprint","IMPRINT",EDGE,{"derivedFrom":sQuery(id+"F15.wireOp",EDGE,"E30.0.3.0")}),1.0]])]});
            var Q4;
            Q4=makeQuery(id+"F15.imprint","IMPRINT",FACE,{"disambiguationData":[TD([[makeQuery(id+"F15.imprint","IMPRINT",EDGE,{"derivedFrom":sQuery(id+"F15.wireOp",EDGE,"E30.0.4.0")}),1.0]])]});
            var Q5;
            Q5=makeQuery(id+"F15.imprint","IMPRINT",FACE,{"disambiguationData":[TD([[makeQuery(id+"F15.imprint","IMPRINT",EDGE,{"derivedFrom":sQuery(id+"F15.wireOp",EDGE,"E30.0.5.0")}),1.0]])]});
            var Q6;
            Q6=makeQuery(id+"F15.imprint","IMPRINT",FACE,{"disambiguationData":[TD([[makeQuery(id+"F15.imprint","IMPRINT",EDGE,{"derivedFrom":sQuery(id+"F15.wireOp",EDGE,"E30.0.6.0")}),1.0]])]});
            var Q7;
            Q7=makeQuery(id+"F15.imprint","IMPRINT",FACE,{"disambiguationData":[TD([[makeQuery(id+"F15.imprint","IMPRINT",EDGE,{"derivedFrom":sQuery(id+"F15.wireOp",EDGE,"E30.0.7.0")}),1.0]])]});
            extrude(context, id + "F16", {"entities" : qUnion([Q0, Q1, Q2, Q3, Q4, Q5, Q6, Q7]), "operationType" : NewBodyOperationType.REMOVE, "oppositeDirection" : true, "depth" : .25 * mm});
        }
        {
            var Q0;
            {var subQ0=sQuery(id+"F0.wireOp",EDGE,"E5.4");Q0=makeQuery(id+"FrbD3DidOZEMZMG_1.boolean.opBoolean","MERGE",FACE,{"derivedFrom":[makeQuery(id+"F1.opExtrude","SWEPT_FACE",FACE,{"disambiguationData":[OSD([subQ0])]}),makeQuery(id+"FrbD3DidOZEMZMG_1.opExtrude","SWEPT_FACE",FACE,{"disambiguationData":[OSD([subQ0])]})]});}
            var sketch = newSketch(context, id + "F17", { "sketchPlane" : qUnion([Q0])});
            skLineSegment(sketch, "E31", {"start": v(-5.27, 48.25) * mm, "end": v(5.27, 48.25) * mm});
            skArc(sketch, "E32", {"start": v(5.27, 43.75) * mm, "mid": v(7.52, 46) * mm, "end": v(5.27, 48.25) * mm});
            skLineSegment(sketch, "E33", {"start": v(5.27, 43.75) * mm, "end": v(-5.27, 43.75) * mm});
            skArc(sketch, "E34", {"start": v(-5.27, 48.25) * mm, "mid": v(-7.52, 46) * mm, "end": v(-5.27, 43.75) * mm});
            skArc(sketch, "E35.0.1.0", {"start": v(-5.27, 42.25) * mm, "mid": v(-7.52, 40) * mm, "end": v(-5.27, 37.75) * mm});
            skLineSegment(sketch, "E35.0.1.1", {"start": v(-5.27, 42.25) * mm, "end": v(5.27, 42.25) * mm});
            skArc(sketch, "E35.0.1.2", {"start": v(5.27, 37.75) * mm, "mid": v(7.52, 40) * mm, "end": v(5.27, 42.25) * mm});
            skLineSegment(sketch, "E35.0.1.3", {"start": v(5.27, 37.75) * mm, "end": v(-5.27, 37.75) * mm});
            skArc(sketch, "E35.0.2.0", {"start": v(-5.27, 36.25) * mm, "mid": v(-7.52, 34) * mm, "end": v(-5.27, 31.75) * mm});
            skLineSegment(sketch, "E35.0.2.1", {"start": v(-5.27, 36.25) * mm, "end": v(5.27, 36.25) * mm});
            skArc(sketch, "E35.0.2.2", {"start": v(5.27, 31.75) * mm, "mid": v(7.52, 34) * mm, "end": v(5.27, 36.25) * mm});
            skLineSegment(sketch, "E35.0.2.3", {"start": v(5.27, 31.75) * mm, "end": v(-5.27, 31.75) * mm});
            skArc(sketch, "E35.0.3.0", {"start": v(-5.27, 30.25) * mm, "mid": v(-7.52, 28) * mm, "end": v(-5.27, 25.75) * mm});
            skLineSegment(sketch, "E35.0.3.1", {"start": v(-5.27, 30.25) * mm, "end": v(5.27, 30.25) * mm});
            skArc(sketch, "E35.0.3.2", {"start": v(5.27, 25.75) * mm, "mid": v(7.52, 28) * mm, "end": v(5.27, 30.25) * mm});
            skLineSegment(sketch, "E35.0.3.3", {"start": v(5.27, 25.75) * mm, "end": v(-5.27, 25.75) * mm});
            skArc(sketch, "E35.0.4.0", {"start": v(-5.27, 24.25) * mm, "mid": v(-7.52, 22) * mm, "end": v(-5.27, 19.75) * mm});
            skLineSegment(sketch, "E35.0.4.1", {"start": v(-5.27, 24.25) * mm, "end": v(5.27, 24.25) * mm});
            skArc(sketch, "E35.0.4.2", {"start": v(5.27, 19.75) * mm, "mid": v(7.52, 22) * mm, "end": v(5.27, 24.25) * mm});
            skLineSegment(sketch, "E35.0.4.3", {"start": v(5.27, 19.75) * mm, "end": v(-5.27, 19.75) * mm});
            skArc(sketch, "E35.0.5.0", {"start": v(-5.27, 18.25) * mm, "mid": v(-7.52, 16) * mm, "end": v(-5.27, 13.75) * mm});
            skLineSegment(sketch, "E35.0.5.1", {"start": v(-5.27, 18.25) * mm, "end": v(5.27, 18.25) * mm});
            skArc(sketch, "E35.0.5.2", {"start": v(5.27, 13.75) * mm, "mid": v(7.52, 16) * mm, "end": v(5.27, 18.25) * mm});
            skLineSegment(sketch, "E35.0.5.3", {"start": v(5.27, 13.75) * mm, "end": v(-5.27, 13.75) * mm});
            skArc(sketch, "E35.0.6.0", {"start": v(-5.27, 12.25) * mm, "mid": v(-7.52, 10) * mm, "end": v(-5.27, 7.75) * mm});
            skLineSegment(sketch, "E35.0.6.1", {"start": v(-5.27, 12.25) * mm, "end": v(5.27, 12.25) * mm});
            skArc(sketch, "E35.0.6.2", {"start": v(5.27, 7.75) * mm, "mid": v(7.52, 10) * mm, "end": v(5.27, 12.25) * mm});
            skLineSegment(sketch, "E35.0.6.3", {"start": v(5.27, 7.75) * mm, "end": v(-5.27, 7.75) * mm});
            skArc(sketch, "E35.0.7.0", {"start": v(-5.27, 6.25) * mm, "mid": v(-7.52, 4) * mm, "end": v(-5.27, 1.75) * mm});
            skLineSegment(sketch, "E35.0.7.1", {"start": v(-5.27, 6.25) * mm, "end": v(5.27, 6.25) * mm});
            skArc(sketch, "E35.0.7.2", {"start": v(5.27, 1.75) * mm, "mid": v(7.52, 4) * mm, "end": v(5.27, 6.25) * mm});
            skLineSegment(sketch, "E35.0.7.3", {"start": v(5.27, 1.75) * mm, "end": v(-5.27, 1.75) * mm});
            skLineSegment(sketch, "E35.direction1", {"start": v(-5.27, 43.75) * mm, "end": v(18.93, 43.75) * mm, "construction": true});
            skLineSegment(sketch, "E35.direction2", {"start": v(-5.27, 43.75) * mm, "end": v(-5.27, 37.75) * mm, "construction": true});
            skSolve(sketch);
        }
        {
            var Q0;
            Q0=makeQuery(id+"F17.imprint","IMPRINT",FACE,{"disambiguationData":[TD([[makeQuery(id+"F17.imprint","IMPRINT",EDGE,{"derivedFrom":sQuery(id+"F17.wireOp",EDGE,"E31")}),-1.0]])]});
            var Q1;
            Q1=makeQuery(id+"F17.imprint","IMPRINT",FACE,{"disambiguationData":[TD([[makeQuery(id+"F17.imprint","IMPRINT",EDGE,{"derivedFrom":sQuery(id+"F17.wireOp",EDGE,"E35.0.1.0")}),1.0]])]});
            var Q2;
            Q2=makeQuery(id+"F17.imprint","IMPRINT",FACE,{"disambiguationData":[TD([[makeQuery(id+"F17.imprint","IMPRINT",EDGE,{"derivedFrom":sQuery(id+"F17.wireOp",EDGE,"E35.0.2.0")}),1.0]])]});
            var Q3;
            Q3=makeQuery(id+"F17.imprint","IMPRINT",FACE,{"disambiguationData":[TD([[makeQuery(id+"F17.imprint","IMPRINT",EDGE,{"derivedFrom":sQuery(id+"F17.wireOp",EDGE,"E35.0.3.0")}),1.0]])]});
            var Q4;
            Q4=makeQuery(id+"F17.imprint","IMPRINT",FACE,{"disambiguationData":[TD([[makeQuery(id+"F17.imprint","IMPRINT",EDGE,{"derivedFrom":sQuery(id+"F17.wireOp",EDGE,"E35.0.4.0")}),1.0]])]});
            var Q5;
            Q5=makeQuery(id+"F17.imprint","IMPRINT",FACE,{"disambiguationData":[TD([[makeQuery(id+"F17.imprint","IMPRINT",EDGE,{"derivedFrom":sQuery(id+"F17.wireOp",EDGE,"E35.0.5.0")}),1.0]])]});
            var Q6;
            Q6=makeQuery(id+"F17.imprint","IMPRINT",FACE,{"disambiguationData":[TD([[makeQuery(id+"F17.imprint","IMPRINT",EDGE,{"derivedFrom":sQuery(id+"F17.wireOp",EDGE,"E35.0.6.0")}),1.0]])]});
            var Q7;
            Q7=makeQuery(id+"F17.imprint","IMPRINT",FACE,{"disambiguationData":[TD([[makeQuery(id+"F17.imprint","IMPRINT",EDGE,{"derivedFrom":sQuery(id+"F17.wireOp",EDGE,"E35.0.7.0")}),1.0]])]});
            extrude(context, id + "F18", {"entities" : qUnion([Q0, Q1, Q2, Q3, Q4, Q5, Q6, Q7]), "operationType" : NewBodyOperationType.REMOVE, "oppositeDirection" : true, "depth" : .25 * mm});
        }
    });
